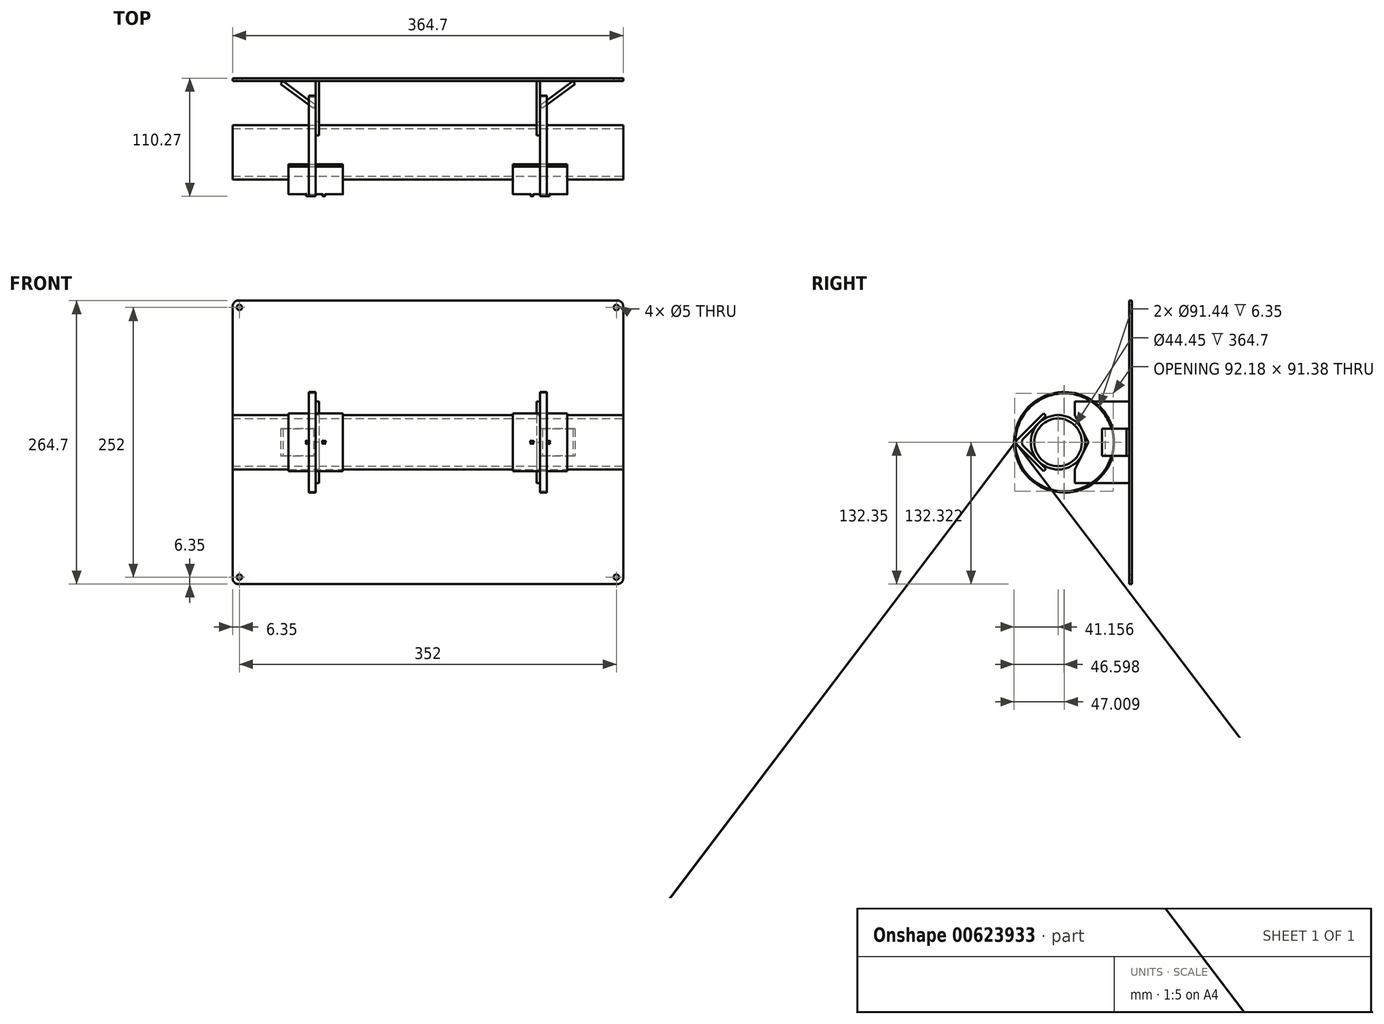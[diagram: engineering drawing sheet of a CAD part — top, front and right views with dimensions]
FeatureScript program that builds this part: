
annotation { "Feature Type Name" : "Feature", "Feature Type Description" : "" }
export const myFeature = defineFeature(function(context is Context, id is Id, definition is map)
    precondition{}
    {
        {
            var Q0;
            Q0=qCreatedBy(makeId("Front.planeOp"),FACE);
            var sketch = newSketch(context, id + "F0", { "sketchPlane" : qUnion([Q0])});
            skLineSegment(sketch, "E0.bottom", {"start": v(0, 0) * mm, "end": v(364.7, 0) * mm});
            skLineSegment(sketch, "E0.top", {"start": v(0, 264.7) * mm, "end": v(364.7, 264.7) * mm});
            skLineSegment(sketch, "E0.left", {"start": v(0, 0) * mm, "end": v(0, 264.7) * mm});
            skLineSegment(sketch, "E0.right", {"start": v(364.7, 0) * mm, "end": v(364.7, 264.7) * mm});
            skLineSegment(sketch, "E1.bottom", {"start": v(6.35, 6.35) * mm, "end": v(358.35, 6.35) * mm, "construction": true});
            skLineSegment(sketch, "E1.top", {"start": v(6.35, 258.35) * mm, "end": v(358.35, 258.35) * mm, "construction": true});
            skLineSegment(sketch, "E1.left", {"start": v(6.35, 6.35) * mm, "end": v(6.35, 258.35) * mm, "construction": true});
            skLineSegment(sketch, "E1.right", {"start": v(358.35, 6.35) * mm, "end": v(358.35, 258.35) * mm, "construction": true});
            skCircle(sketch, "E2", {"center": v(358.35, 258.35) * mm, "radius": 2.5 * mm});
            skCircle(sketch, "E3", {"center": v(6.35, 258.35) * mm, "radius": 2.5 * mm});
            skCircle(sketch, "E4", {"center": v(6.35, 6.35) * mm, "radius": 2.5 * mm});
            skCircle(sketch, "E5", {"center": v(358.35, 6.35) * mm, "radius": 2.5 * mm});
            skSolve(sketch);
        }
        {
            var Q0;
            Q0=qSketchRegion(id+"F0",true);
            extrude(context, id + "F1", {"entities" : qUnion([Q0]), "depth" : 2.62 * mm, "offsetDistance" : 25.4 * mm});
        }
        {
            var Q0;
            Q0=makeQuery(id+"F1.opExtrude","SWEPT_EDGE",EDGE,{"disambiguationData":[OSD([sQuery(id+"F0.wireOp",EDGE,"E0.top"),sQuery(id+"F0.wireOp",EDGE,"E0.right")])]});
            var Q1;
            Q1=makeQuery(id+"F1.opExtrude","SWEPT_EDGE",EDGE,{"disambiguationData":[OSD([sQuery(id+"F0.wireOp",EDGE,"E0.bottom"),sQuery(id+"F0.wireOp",EDGE,"E0.right")])]});
            var Q2;
            Q2=makeQuery(id+"F1.opExtrude","SWEPT_EDGE",EDGE,{"disambiguationData":[OSD([sQuery(id+"F0.wireOp",EDGE,"E0.bottom"),sQuery(id+"F0.wireOp",EDGE,"E0.left")])]});
            var Q3;
            Q3=makeQuery(id+"F1.opExtrude","SWEPT_EDGE",EDGE,{"disambiguationData":[OSD([sQuery(id+"F0.wireOp",EDGE,"E0.top"),sQuery(id+"F0.wireOp",EDGE,"E0.left")])]});
            fillet(context, id + "F2", {"entities" : qUnion([Q0, Q1, Q2, Q3]), "radius" : 5.08 * mm, "tangentPropagation" : true, "allowEdgeOverflow" : false});
        }
        {
            var Q0;
            Q0=makeQuery(id+"F1.opExtrude","SWEPT_FACE",FACE,{"disambiguationData":[OSD([sQuery(id+"F0.wireOp",EDGE,"E0.left")])]});
            var Q1;
            Q1=makeQuery(id+"F1.opExtrude","SWEPT_FACE",FACE,{"disambiguationData":[OSD([sQuery(id+"F0.wireOp",EDGE,"E0.right")])]});
            cPlane(context, id + "F3", {"entities" : qUnion([Q0, Q1]), "cplaneType" : CPlaneType.MID_PLANE, "offset" : 25.4 * mm, "width" : 152.4 * mm, "height" : 152.4 * mm});
        }
        {
            var Q0;
            Q0=makeQuery(id+"F1.opExtrude","CAP_FACE",FACE,{"disambiguationData":[OSD([sQuery(id+"F0.wireOp",EDGE,"E0.bottom"),sQuery(id+"F0.wireOp",EDGE,"E0.top"),sQuery(id+"F0.wireOp",EDGE,"E0.left"),sQuery(id+"F0.wireOp",EDGE,"E0.right"),sQuery(id+"F0.wireOp",EDGE,"E2"),sQuery(id+"F0.wireOp",EDGE,"E3"),sQuery(id+"F0.wireOp",EDGE,"E4"),sQuery(id+"F0.wireOp",EDGE,"E5")])],"isStart":false});
            var sketch = newSketch(context, id + "F4", { "sketchPlane" : qUnion([Q0])});
            skLineSegment(sketch, "E6.bottom", {"start": v(287.12, 170.45) * mm, "end": v(283.95, 170.45) * mm});
            skLineSegment(sketch, "E6.top", {"start": v(287.12, 94.25) * mm, "end": v(283.95, 94.25) * mm});
            skLineSegment(sketch, "E6.left", {"start": v(287.12, 170.45) * mm, "end": v(287.12, 94.25) * mm});
            skLineSegment(sketch, "E6.right", {"start": v(283.95, 170.45) * mm, "end": v(283.95, 94.25) * mm});
            skLineSegment(sketch, "E7", {"start": v(287.12, 132.35) * mm, "end": v(364.7, 132.35) * mm, "construction": true});
            skLineSegment(sketch, "E8", {"start": v(182.35, 94.25) * mm, "end": v(182.35, 0) * mm, "construction": true});
            skLineSegment(sketch, "E9.MirrorCS", {"start": v(77.57, 170.45) * mm, "end": v(80.75, 170.45) * mm, "construction": true});
            skLineSegment(sketch, "E10.MirrorCS", {"start": v(77.57, 94.25) * mm, "end": v(80.75, 94.25) * mm, "construction": true});
            skLineSegment(sketch, "E11.MirrorCS", {"start": v(80.75, 170.45) * mm, "end": v(80.75, 94.25) * mm, "construction": true});
            skLineSegment(sketch, "E12.MirrorCS", {"start": v(77.57, 170.45) * mm, "end": v(77.57, 94.25) * mm, "construction": true});
            skSolve(sketch);
        }
        {
            var Q0;
            Q0=qSketchRegion(id+"F4",true);
            extrude(context, id + "F5", {"entities" : qUnion([Q0]), "depth" : 50.8 * mm, "offsetDistance" : 25.4 * mm});
        }
        {
            var Q0;
            Q0=makeQuery(id+"F5.opExtrude","SWEPT_FACE",FACE,{"disambiguationData":[OSD([sQuery(id+"F4.wireOp",EDGE,"E6.left")])]});
            var sketch = newSketch(context, id + "F6", { "sketchPlane" : qUnion([Q0])});
            skLineSegment(sketch, "E13", {"start": v(-53.42, 157.75) * mm, "end": v(-40.72, 132.35) * mm});
            skLineSegment(sketch, "E14", {"start": v(-40.72, 132.35) * mm, "end": v(-53.42, 106.95) * mm});
            skLineSegment(sketch, "E15", {"start": v(-53.42, 106.95) * mm, "end": v(-53.42, 157.75) * mm});
            skCircle(sketch, "E16", {"center": v(-69.11, 132.35) * mm, "radius": 25.4 * mm, "construction": true});
            skSolve(sketch);
        }
        {
            var Q0;
            Q0=qSketchRegion(id+"F6",true);
            extrude(context, id + "F7", {"entities" : qUnion([Q0]), "operationType" : NewBodyOperationType.REMOVE, "endBound" : BoundingType.THROUGH_ALL, "oppositeDirection" : true, "depth" : 25.4 * mm, "offsetDistance" : 25.4 * mm});
        }
        {
            var Q0;
            Q0=makeQuery(id+"F1.opExtrude","SWEPT_FACE",FACE,{"disambiguationData":[OSD([sQuery(id+"F0.wireOp",EDGE,"E0.top")])]});
            var Q1;
            Q1=makeQuery(id+"F1.opExtrude","SWEPT_FACE",FACE,{"disambiguationData":[OSD([sQuery(id+"F0.wireOp",EDGE,"E0.bottom")])]});
            cPlane(context, id + "F8", {"entities" : qUnion([Q0, Q1]), "cplaneType" : CPlaneType.MID_PLANE, "offset" : 25.4 * mm, "width" : 152.4 * mm, "height" : 152.4 * mm});
        }
        {
            var Q0;
            Q0=qCreatedBy(id+"F8.planeOp",FACE);
            var sketch = newSketch(context, id + "F9", { "sketchPlane" : qUnion([Q0])});
            skLineSegment(sketch, "E17", {"start": v(287.12, -25.26) * mm, "end": v(317.77, -2.62) * mm});
            skLineSegment(sketch, "E18", {"start": v(317.77, -2.62) * mm, "end": v(319.8, -5.37) * mm});
            skLineSegment(sketch, "E19", {"start": v(319.8, -5.37) * mm, "end": v(289.16, -28.02) * mm});
            skLineSegment(sketch, "E20", {"start": v(289.16, -28.02) * mm, "end": v(287.12, -25.26) * mm});
            skLineSegment(sketch, "E21", {"start": v(182.35, -51.04) * mm, "end": v(182.35, -2.62) * mm, "construction": true});
            skSolve(sketch);
        }
        {
            var Q0;
            Q0=qSketchRegion(id+"F9",true);
            extrude(context, id + "F10", {"entities" : qUnion([Q0]), "endBound" : BoundingType.SYMMETRIC, "depth" : 25.4 * mm, "offsetDistance" : 25.4 * mm});
        }
        {
            var Q0;
            Q0=makeQuery(id+"F1.opExtrude","SWEPT_FACE",FACE,{"disambiguationData":[OSD([sQuery(id+"F0.wireOp",EDGE,"E0.right")])]});
            var sketch = newSketch(context, id + "F11", { "sketchPlane" : qUnion([Q0])});
            skCircle(sketch, "E22", {"center": v(-69.11, 132.35) * mm, "radius": 25.4 * mm});
            skCircle(sketch, "E23", {"center": v(-69.11, 132.35) * mm, "radius": 22.23 * mm});
            skSolve(sketch);
        }
        {
            var Q0;
            Q0=qSketchRegion(id+"F11",true);
            var Q1;
            Q1=makeQuery(id+"F1.opExtrude","SWEPT_FACE",FACE,{"disambiguationData":[OSD([sQuery(id+"F0.wireOp",EDGE,"E0.left")])]});
            extrude(context, id + "F12", {"entities" : qUnion([Q0]), "endBound" : BoundingType.UP_TO_SURFACE, "oppositeDirection" : true, "depth" : 25.4 * mm, "endBoundEntityFace" : qUnion([Q1]), "offsetDistance" : 25.4 * mm});
        }
        {
            var Q0;
            Q0=makeQuery(id+"F5.opExtrude","SWEPT_FACE",FACE,{"disambiguationData":[OSD([sQuery(id+"F4.wireOp",EDGE,"E6.left")])]});
            var sketch = newSketch(context, id + "F13", { "sketchPlane" : qUnion([Q0])});
            skLineSegment(sketch, "E24", {"start": v(-80.34, 157.05) * mm, "end": v(-105.04, 132.35) * mm});
            skLineSegment(sketch, "E25", {"start": v(-105.04, 132.35) * mm, "end": v(-80.34, 107.65) * mm});
            skLineSegment(sketch, "E26", {"start": v(-80.34, 107.65) * mm, "end": v(-82.58, 105.4) * mm});
            skLineSegment(sketch, "E27", {"start": v(-82.58, 105.4) * mm, "end": v(-109.53, 132.35) * mm});
            skLineSegment(sketch, "E28", {"start": v(-109.53, 132.35) * mm, "end": v(-82.58, 159.3) * mm});
            skLineSegment(sketch, "E29", {"start": v(-82.58, 159.3) * mm, "end": v(-80.34, 157.05) * mm});
            skLineSegment(sketch, "E30", {"start": v(-69.11, 132.35) * mm, "end": v(-105.04, 132.35) * mm, "construction": true});
            skSolve(sketch);
        }
        {
            var Q0;
            Q0=qSketchRegion(id+"F13",true);
            extrude(context, id + "F14", {"entities" : qUnion([Q0]), "operationType" : NewBodyOperationType.ADD, "depth" : 25.4 * mm, "offsetDistance" : 25.4 * mm, "hasSecondDirection" : true, "secondDirectionOppositeDirection" : true, "secondDirectionDepth" : 25.4 * mm});
        }
        {
            var Q0;
            Q0=makeQuery(id+"F14.opExtrude","SWEPT_EDGE",EDGE,{"disambiguationData":[OSD([sQuery(id+"F13.wireOp",EDGE,"E27"),sQuery(id+"F13.wireOp",EDGE,"E28")])]});
            fillet(context, id + "F15", {"entities" : qUnion([Q0]), "radius" : 2.54 * mm, "tangentPropagation" : true, "allowEdgeOverflow" : false});
        }
        {
            var Q0;
            Q0=makeQuery(id+"F14.opExtrude","SWEPT_EDGE",EDGE,{"disambiguationData":[OSD([sQuery(id+"F13.wireOp",EDGE,"E24"),sQuery(id+"F13.wireOp",EDGE,"E25")])]});
            fillet(context, id + "F16", {"entities" : qUnion([Q0]), "radius" : 5.08 * mm, "tangentPropagation" : true, "allowEdgeOverflow" : false});
        }
        {
            var Q0;
            Q0=qCreatedBy(id+"F8.planeOp",FACE);
            var sketch = newSketch(context, id + "F17", { "sketchPlane" : qUnion([Q0])});
            skLineSegment(sketch, "E31.bottom", {"start": v(296.01, -107.73) * mm, "end": v(293.47, -107.73) * mm});
            skLineSegment(sketch, "E31.top", {"start": v(296.01, -110.27) * mm, "end": v(293.47, -110.27) * mm});
            skLineSegment(sketch, "E31.left", {"start": v(296.01, -107.73) * mm, "end": v(296.01, -110.27) * mm});
            skLineSegment(sketch, "E31.right", {"start": v(293.47, -107.73) * mm, "end": v(293.47, -110.27) * mm});
            skLineSegment(sketch, "E32", {"start": v(287.12, -82.58) * mm, "end": v(287.12, -92.6) * mm, "construction": true});
            skLineSegment(sketch, "E33.MirrorCS", {"start": v(278.23, -107.73) * mm, "end": v(280.77, -107.73) * mm});
            skLineSegment(sketch, "E34.MirrorCS", {"start": v(278.23, -110.27) * mm, "end": v(280.77, -110.27) * mm});
            skLineSegment(sketch, "E35.MirrorCS", {"start": v(278.23, -107.73) * mm, "end": v(278.23, -110.27) * mm});
            skLineSegment(sketch, "E36.MirrorCS", {"start": v(280.77, -107.73) * mm, "end": v(280.77, -110.27) * mm});
            skSolve(sketch);
        }
        {
            var Q0;
            Q0=qSketchRegion(id+"F17",true);
            extrude(context, id + "F18", {"entities" : qUnion([Q0]), "operationType" : NewBodyOperationType.ADD, "endBound" : BoundingType.SYMMETRIC, "depth" : 2.54 * mm, "offsetDistance" : 25.4 * mm});
        }
        {
            var Q0;
            Q0=makeQuery(id+"F18.boolean.opBoolean","INTERSECT",EDGE,{"derivedFrom":[makeQuery(id+"F15.opFillet","BLEND_FACE",FACE,{"disambiguationData":[OSD([sQuery(id+"F13.wireOp",EDGE,"E27"),sQuery(id+"F13.wireOp",EDGE,"E28")])]}),makeQuery(id+"F18.opExtrude","CAP_FACE",FACE,{"disambiguationData":[OSD([sQuery(id+"F17.wireOp",EDGE,"E31.bottom"),sQuery(id+"F17.wireOp",EDGE,"E31.top"),sQuery(id+"F17.wireOp",EDGE,"E31.left"),sQuery(id+"F17.wireOp",EDGE,"E31.right")])],"isStart":false})]});
            var Q1;
            Q1=makeQuery(id+"F18.opExtrude","SWEPT_FACE",FACE,{"disambiguationData":[OSD([sQuery(id+"F17.wireOp",EDGE,"E31.left")])]});
            var Q2;
            Q2=makeQuery(id+"F18.opExtrude","SWEPT_FACE",FACE,{"disambiguationData":[OSD([sQuery(id+"F17.wireOp",EDGE,"E31.right")])]});
            var Q3;
            Q3=makeQuery(id+"F18.opExtrude","CAP_FACE",FACE,{"disambiguationData":[OSD([sQuery(id+"F17.wireOp",EDGE,"E31.bottom"),sQuery(id+"F17.wireOp",EDGE,"E31.top"),sQuery(id+"F17.wireOp",EDGE,"E31.left"),sQuery(id+"F17.wireOp",EDGE,"E31.right")])],"isStart":true});
            var Q4;
            Q4=makeQuery(id+"F18.opExtrude","CAP_FACE",FACE,{"disambiguationData":[OSD([sQuery(id+"F17.wireOp",EDGE,"E31.bottom"),sQuery(id+"F17.wireOp",EDGE,"E31.top"),sQuery(id+"F17.wireOp",EDGE,"E31.left"),sQuery(id+"F17.wireOp",EDGE,"E31.right")])],"isStart":false});
            var Q5;
            Q5=makeQuery(id+"F18.opExtrude","SWEPT_FACE",FACE,{"disambiguationData":[OSD([sQuery(id+"F17.wireOp",EDGE,"E34.MirrorCS")])]});
            var Q6;
            Q6=makeQuery(id+"F18.opExtrude","CAP_FACE",FACE,{"disambiguationData":[OSD([sQuery(id+"F17.wireOp",EDGE,"E33.MirrorCS"),sQuery(id+"F17.wireOp",EDGE,"E34.MirrorCS"),sQuery(id+"F17.wireOp",EDGE,"E35.MirrorCS"),sQuery(id+"F17.wireOp",EDGE,"E36.MirrorCS")])],"isStart":false});
            var Q7;
            Q7=makeQuery(id+"F18.boolean.opBoolean","INTERSECT",EDGE,{"derivedFrom":[makeQuery(id+"F15.opFillet","BLEND_FACE",FACE,{"disambiguationData":[OSD([sQuery(id+"F13.wireOp",EDGE,"E27"),sQuery(id+"F13.wireOp",EDGE,"E28")])]}),makeQuery(id+"F18.opExtrude","CAP_FACE",FACE,{"disambiguationData":[OSD([sQuery(id+"F17.wireOp",EDGE,"E33.MirrorCS"),sQuery(id+"F17.wireOp",EDGE,"E34.MirrorCS"),sQuery(id+"F17.wireOp",EDGE,"E35.MirrorCS"),sQuery(id+"F17.wireOp",EDGE,"E36.MirrorCS")])],"isStart":true})]});
            fillet(context, id + "F19", {"entities" : qUnion([Q0, Q1, Q2, Q3, Q4, Q5, Q6, Q7]), "radius" : 0.5 * mm, "tangentPropagation" : true, "allowEdgeOverflow" : false});
        }
        {
            var Q0;
            Q0=makeQuery(id+"F5.opExtrude","SWEPT_FACE",FACE,{"disambiguationData":[OSD([sQuery(id+"F4.wireOp",EDGE,"E6.left")])]});
            var sketch = newSketch(context, id + "F20", { "sketchPlane" : qUnion([Q0])});
            skCircle(sketch, "E37", {"center": v(-63.26, 132.35) * mm, "radius": 45.72 * mm});
            skCircle(sketch, "E38", {"center": v(-63.26, 132.35) * mm, "radius": 47 * mm});
            skSolve(sketch);
        }
        {
            var Q0;
            Q0=qSketchRegion(id+"F20",true);
            extrude(context, id + "F21", {"entities" : qUnion([Q0]), "depth" : 6.35 * mm, "offsetDistance" : 25.4 * mm});
        }
        {
            var Q0;
            Q0=makeQuery(id+"F14.opExtrude","SWEPT_BODY",BODY,{"disambiguationData":[OSD([sQuery(id+"F13.wireOp",EDGE,"E24"),sQuery(id+"F13.wireOp",EDGE,"E25"),sQuery(id+"F13.wireOp",EDGE,"E26"),sQuery(id+"F13.wireOp",EDGE,"E27"),sQuery(id+"F13.wireOp",EDGE,"E28"),sQuery(id+"F13.wireOp",EDGE,"E29")])]});
            var Q1;
            Q1=makeQuery(id+"F10.opExtrude","SWEPT_BODY",BODY,{"disambiguationData":[OSD([sQuery(id+"F9.wireOp",EDGE,"E17"),sQuery(id+"F9.wireOp",EDGE,"E18"),sQuery(id+"F9.wireOp",EDGE,"E19"),sQuery(id+"F9.wireOp",EDGE,"E20")])]});
            var Q2;
            Q2=makeQuery(id+"F5.opExtrude","SWEPT_BODY",BODY,{"disambiguationData":[OSD([sQuery(id+"F4.wireOp",EDGE,"E6.bottom"),sQuery(id+"F4.wireOp",EDGE,"E6.top"),sQuery(id+"F4.wireOp",EDGE,"E6.left"),sQuery(id+"F4.wireOp",EDGE,"E6.right")])]});
            var Q3;
            Q3=makeQuery(id+"F21.opExtrude","SWEPT_BODY",BODY,{"disambiguationData":[OSD([sQuery(id+"F20.wireOp",EDGE,"E37"),sQuery(id+"F20.wireOp",EDGE,"E38")])]});
            var Q4;
            Q4=qCreatedBy(id+"F3.planeOp",FACE);
            mirror(context, id + "F22", {"operationType" : NewBodyOperationType.ADD, "entities" : qUnion([Q0, Q1, Q2, Q3]), "mirrorPlane" : qUnion([Q4])});
        }
    });
